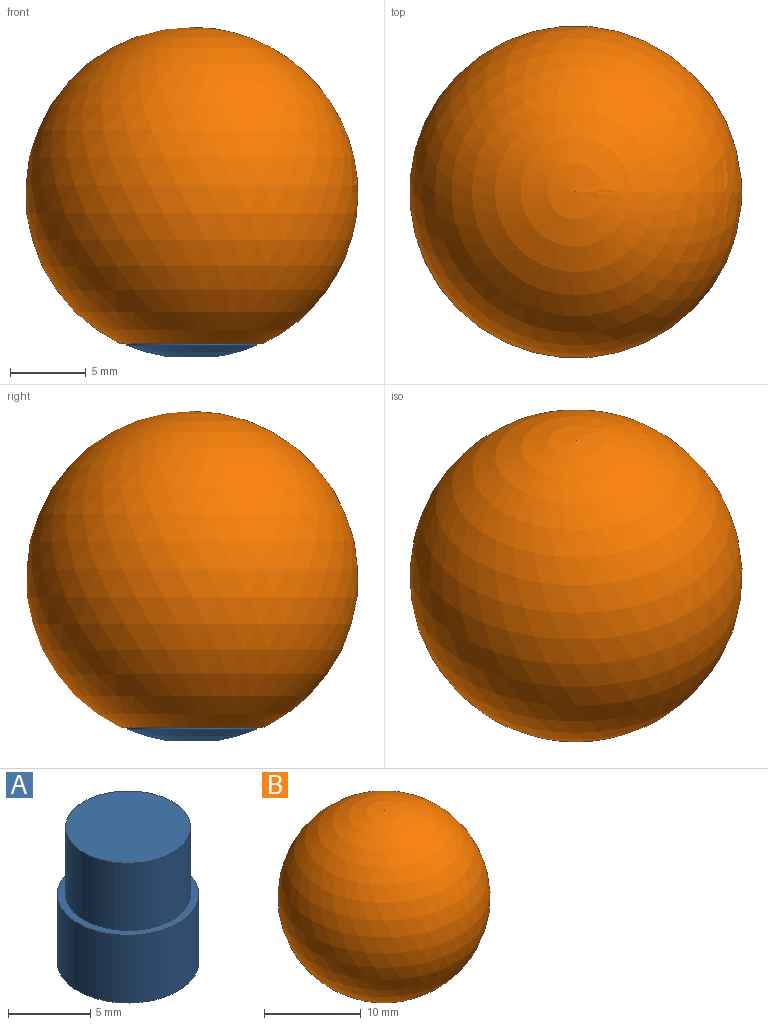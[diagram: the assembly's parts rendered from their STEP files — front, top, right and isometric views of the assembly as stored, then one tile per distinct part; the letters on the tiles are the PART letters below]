
ASSEMBLY  parts=2 mates=1
PART A: 7 faces, bbox 8.6x8.6x10.8 mm
  f0: cylinder r=1.59mm len=6mm, axis (0,0,1), area 59.8mm2, adj f1,f6
  f1: sphere r=10.92mm, area 52.6mm2, adj f0,f2
  f2: cylinder r=4.3mm len=8.6mm, axis (0,0,1), area 136.1mm2, adj f1,f3
  f3: plane 8.6x8.6mm, normal (0,0,1), area 12.7mm2, adj f2,f4
  f4: cylinder r=3.8mm len=7.6mm, axis (0,0,1), area 119.4mm2, adj f3,f5
  f5: plane 7.6x7.6mm, normal (0,0,1), area 45.4mm2, adj f4
  f6: plane 3.18x3.18mm, normal (0,0,-1), area 7.9mm2, adj f0
PART B: 5 faces, bbox 22x22x20.9 mm
  f0: cylinder r=4.7mm len=9.4mm, axis (0,0,1), area 146mm2, adj f1,f4
  f1: sphere r=11mm, area 1447.6mm2, adj f0
  f2: sphere r=4.2mm, area 110.8mm2, adj f3
  f3: cylinder r=4.2mm len=8.4mm, axis (0,0,1), area 131.9mm2, adj f2,f4
  f4: plane 9.4x9.4mm, normal (0,0,-1), area 14mm2, adj f0,f3
PLACE A t=(-0.53,1.84,-23.4)mm
PLACE B t=(-0.53,1.84,-14.33)mm
MATE fastened B.f0 <-> A.f0  axis (0,0,-1) through (-0.53,1.84,-19.33)mm
